# Revit family: Tyco_Valve_DPV_1_GxG_DN100_2B48800101_Native
name_source: partatom
category: Pipe Accessories
revit_build: Autodesk Revit 2016 (Build: 20150220_1215(x64)
units: mm (PartAtom-declared; Revit-internal decimal feet)

## family parameters
Always vertical = Yes
Cut with Voids When Loaded = No
OmniClass Number = 23.65.55.14.17
OmniClass Title = Adjusting/Controlling Valves for Liquid Services
Part Type = Valve - Breaks Into
Round Connector Dimension = Use Diameter
Shared = No
Work Plane-Based = No

## types (1)
- Tyco_Valve_DPV_1_GxG_DN100_2B48800101_Native
    COBie = Yes
    COBie.Component.Description = DPV-1 GxG Trim Valve DPV-1 CE/FM DN100 (114.3mm) (Gmc)
    COBie.Component.Name = Valves:DPV-1 GxG Dry pipe valve
    COBie.Type = Yes
    COBie.Type.AssetType = Fixed
    COBie.Type.Category = Pr_65_54_95_97:Valves
    COBie.Type.DurationUnit = year
    COBie.Type.Manufacturer = Tyco Fire Protection Products
    COBie.Type.Material = Ductile Iron
    COBie.Type.ModelNumber = 2B48800101
    COBie.Type.ModelReference = DPV-1 GxG Trim Valve DPV-1 CE/FM DN100 (114.3mm) (Gmc)
    COBie.Type.NominalHeight = 0 mm  [stored 0 ft]
    COBie.Type.NominalLength = 0 mm  [stored 0 ft]
    COBie.Type.NominalWidth = 0 mm  [stored 0 ft]
    COBie.Type.ReplacementCost = 0 $
    COBie.Type.Size = DN100 (114.3mm) x DN100 (114.3mm)
    COBie.Type.WarrantyGuarantorParts = http://tycofsbp.com
    Description = DN100 (114.3mm) DPV-1 CE/FM GxG Trim Valve
    Finish_ = Tyco - Paint
    Flange Diameter 1 = 0 mm
    Flange Diameter 2 = 0 mm
    Length X = 346 mm
    Length Y = 0 mm
    Manufacturer = Tyco Fire Protection Products
    Manufacturer URL = www.tyco-fire.com
    Material_ = Ductile Iron
    Model = DPV-1 GxG FM DN100 Trim
    Nominal Diameter 1 = 100 mm
    Nominal Diameter 2 = 100 mm
    Outside Diameter 1 = 114 mm
    Outside Diameter 2 = 114 mm
    Part No = 2B48800101
    Style Id = 0
    Takeout 1 = 0 mm
    Takeout 2 = 0 mm
    Technical Data Sheet No = TFP1090

note: [stored X ft] marks values corroborated as IEEE doubles in the binary element streams (Revit-internal decimal feet)

## geometry (parser evidence)
native form markers: Blend x2, Sweep x109
no freeform markers — native parametric forms only
